# Revit family: TY1234
name_source: partatom
category: Sprinklers
revit_build: Autodesk Revit 2016 (Build: 20150220_1215(x64)
units: mm (PartAtom-declared; Revit-internal decimal feet)

## family parameters
Always vertical = Yes
Cut with Voids When Loaded = No
Maintain Annotation Orientation = No
OmniClass Number = 23.65.70.17.11.24
OmniClass Title = Fire Fighting Sprinkler Heads
Part Type = Normal
Room Calculation Point = No
Round Connector Dimension = Use Diameter
Shared = No
Work Plane-Based = No

## types (6) — shared parameters
COBie = Yes
COBie.Type = Yes
COBie.Type.AssetType = Fixed
COBie.Type.Category = Pr_70_55_97_84:Sprinklers
COBie.Type.DurationUnit = year
COBie.Type.Manufacturer = Tyco Fire Protection Products
COBie.Type.Material = Brass
COBie.Type.NominalHeight = 0' - 0"
COBie.Type.NominalLength = 0' - 0"
COBie.Type.NominalWidth = 0' - 0"
COBie.Type.Shape = Cylinder
COBie.Type.Size = 1/2"(DN15)
COBie.Type.WarrantyGuarantorParts = http://tycofsbp.com
Coverage = Standard
K-Factor = 2.9827
Manufacturer = Tyco Fire Protection Products
Manufacturer URL = www.tyco-fire.com
Model = LFII
Nominal Diameter 1 = 1"
Orifice = Standard
Orifice Size = 0"
Outside Diameter 1 = 1"
Response = Quick
SIN No = TY1234
Takeout 1 = 2"
Technical Data Sheet No = TFP402
zero-valued in all types: COBie.Type.ReplacementCost, Style Id

## per-type parameters (varying)
| type | COBie.Component.Description | COBie.Component.Name | COBie.Type.Colour | COBie.Type.Finish | COBie.Type.ModelNumber | COBie.Type.ModelReference | Part No | Temperature Rating |
| LF II - Low Flow Pendent, Fast Response 1/2" NPT K=3.0 155°F/68°C Brass TY1234 TFP402_51-010-1-155 | LFII Wet Pendent  68.3°C K43 DN15 NPT Br | Sprinklers:Pendent_155 | Yellow | Natural Brass | 51-010-1-155 | LFII Wet Pendent  68.3°C K43 DN15 NPT Br | 51-010-1-155 | 155 °F |
| LF II - Low Flow Pendent, Fast Response 1/2" NPT K=3.0 175°F/79°C Brass TY1234 TFP402_51-010-1-175 | LFII Wet Pendent  79.4°C K43 DN15 NPT Br | Sprinklers:Pendent_175 | Yellow | Natural Brass | 51-010-1-175 | LFII Wet Pendent  79.4°C K43 DN15 NPT Br | 51-010-1-175 | 175 °F |
| LF II - Low Flow Pendent, Fast Response 1/2" NPT K=3.0 155°F/68°C White TY1234 TFP402_51-010-4-155 | LFII Wet Pendent  68.3°C K43 DN15 NPT Wh | Sprinklers:Pendent_155 | White | Signal White | 51-010-4-155 | LFII Wet Pendent  68.3°C K43 DN15 NPT Wh | 51-010-4-155 | 155 °F |
| LF II - Low Flow Pendent, Fast Response 1/2" NPT K=3.0 175°F/79°C White TY1234 TFP402_51-010-4-175 | LFII Wet Pendent  79.4°C K43 DN15 NPT Wh | Sprinklers:Pendent_175 | White | Signal White | 51-010-4-175 | LFII Wet Pendent  79.4°C K43 DN15 NPT Wh | 51-010-4-175 | 175 °F |
| LF II - Low Flow Pendent, Fast Response 1/2" NPT K=3.0 155°F/68°C Chrome TY1234 TFP402_51-010-9-155 | LFII Wet Pendent  68.3°C K43 DN15 NPT Chr | Sprinklers:Pendent_155 | Silver | Chrome Plated | 51-010-9-155 | LFII Wet Pendent  68.3°C K43 DN15 NPT Chr | 51-010-9-155 | 155 °F |
| LF II - Low Flow Pendent, Fast Response 1/2" NPT K=3.0 175°F/79°C Chrome TY1234 TFP402_51-010-9-175 | LFII Wet Pendent  79.4°C K43 DN15 NPT Chr | Sprinklers:Pendent_175 | Silver | Chrome Plated | 51-010-9-175 | LFII Wet Pendent  79.4°C K43 DN15 NPT Chr | 51-010-9-175 | 175 °F |

note: column(s) folded — value = type name in every type: Description

## geometry (parser evidence)
native form markers: Blend x4, Sweep x47
no freeform markers — native parametric forms only
